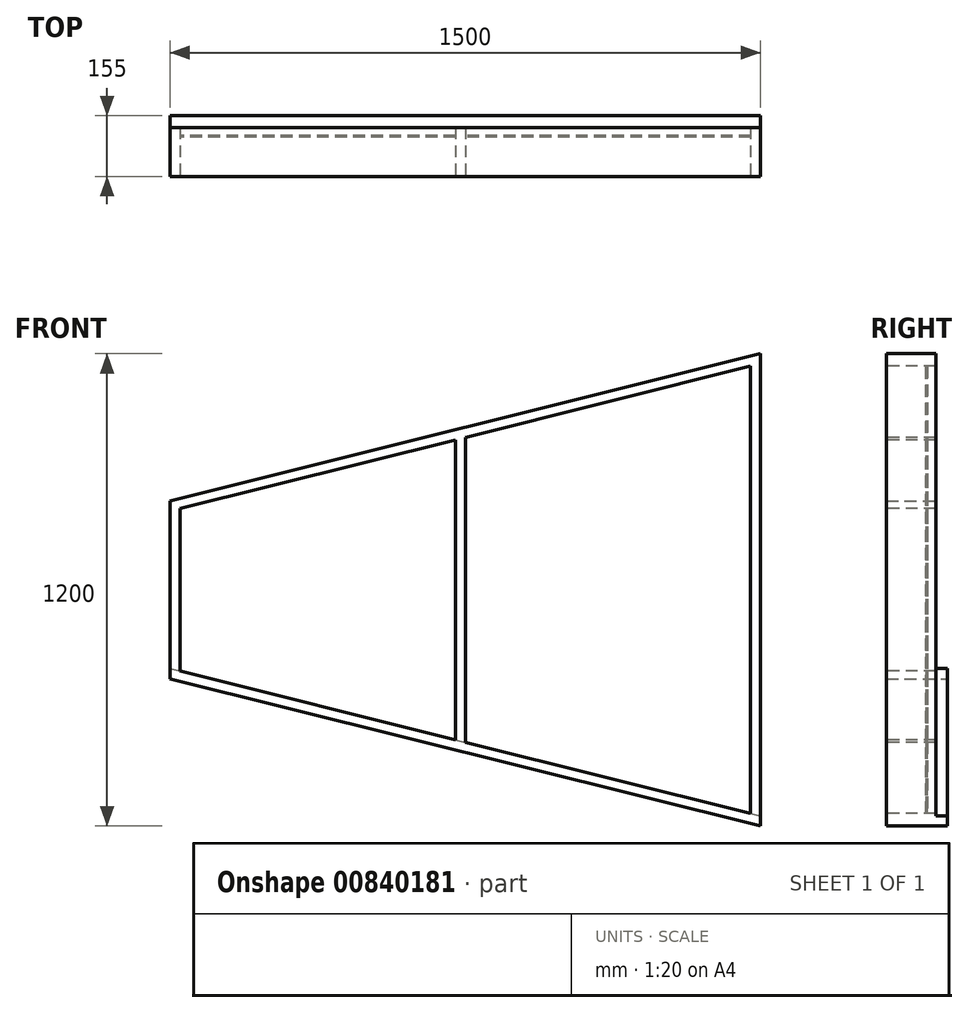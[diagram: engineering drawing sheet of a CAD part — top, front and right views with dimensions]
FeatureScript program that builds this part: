
annotation { "Feature Type Name" : "Feature", "Feature Type Description" : "" }
export const myFeature = defineFeature(function(context is Context, id is Id, definition is map)
    precondition{}
    {
        {
            var Q0;
            Q0=qCreatedBy(makeId("Front.planeOp"),FACE);
            var sketch = newSketch(context, id + "F0", { "sketchPlane" : qUnion([Q0])});
            skLineSegment(sketch, "E0", {"start": v(0, 0) * mm, "end": v(0, 1200) * mm});
            skLineSegment(sketch, "E1", {"start": v(0, 1200) * mm, "end": v(-1500, 826) * mm});
            skLineSegment(sketch, "E2", {"start": v(-1500, 826) * mm, "end": v(-1500, 374) * mm});
            skLineSegment(sketch, "E3", {"start": v(-1500, 374) * mm, "end": v(0, 0) * mm});
            skSolve(sketch);
        }
        {
            var Q0;
            Q0 = qSketchRegion(id + "F0", true);
            extrude(context, id + "F1", {"entities" : qUnion([Q0]), "depth" : 125 * mm, "offsetDistance" : 25 * mm});
        }
        {
            var Q0;
            Q0=makeQuery(id+"F1.opExtrude","CAP_FACE",FACE,{"disambiguationData":[OSD([sQuery(id+"F0.wireOp",EDGE,"E0"),sQuery(id+"F0.wireOp",EDGE,"E1"),sQuery(id+"F0.wireOp",EDGE,"E2"),sQuery(id+"F0.wireOp",EDGE,"E3")])],"isStart":false});
            var sketch = newSketch(context, id + "F2", { "sketchPlane" : qUnion([Q0])});
            skLineSegment(sketch, "E4.0", {"start": v(-25, 1168) * mm, "end": v(-750, 987.24) * mm});
            skLineSegment(sketch, "E4.1", {"start": v(-25, 32) * mm, "end": v(-25, 1168) * mm});
            skLineSegment(sketch, "E4.2", {"start": v(-1475, 393.52) * mm, "end": v(-775, 219) * mm});
            skLineSegment(sketch, "E4.3", {"start": v(-1475, 806.48) * mm, "end": v(-1475, 393.52) * mm});
            skLineSegment(sketch, "E5", {"start": v(-775, 981) * mm, "end": v(-775, 219) * mm});
            skLineSegment(sketch, "E6", {"start": v(-750, 987.24) * mm, "end": v(-750, 212.76) * mm});
            skLineSegment(sketch, "E7.trimOffspring", {"start": v(-775, 981) * mm, "end": v(-1475, 806.48) * mm});
            skLineSegment(sketch, "E8.trimOffspring", {"start": v(-750, 212.76) * mm, "end": v(-25, 32) * mm});
            skSolve(sketch);
        }
        {
            var Q0;
            Q0 = qSketchRegion(id + "F2", true);
            extrude(context, id + "F3", {"entities" : qUnion([Q0]), "operationType" : NewBodyOperationType.REMOVE, "oppositeDirection" : true, "depth" : 50 * mm, "offsetDistance" : 25 * mm});
        }
        {
            var Q0;
            Q0=makeQuery(id+"F1.opExtrude","CAP_FACE",FACE,{"disambiguationData":[OSD([sQuery(id+"F0.wireOp",EDGE,"E0"),sQuery(id+"F0.wireOp",EDGE,"E1"),sQuery(id+"F0.wireOp",EDGE,"E2"),sQuery(id+"F0.wireOp",EDGE,"E3")])],"isStart":true});
            var sketch = newSketch(context, id + "F4", { "sketchPlane" : qUnion([Q0])});
            skLineSegment(sketch, "E9.0", {"start": v(25, 1168) * mm, "end": v(750, 987.24) * mm});
            skLineSegment(sketch, "E9.1", {"start": v(25, 32) * mm, "end": v(25, 1168) * mm});
            skLineSegment(sketch, "E9.2", {"start": v(1475, 393.52) * mm, "end": v(775, 219) * mm});
            skLineSegment(sketch, "E9.3", {"start": v(1475, 806.48) * mm, "end": v(1475, 393.52) * mm});
            skLineSegment(sketch, "E9.4", {"start": v(775, 981) * mm, "end": v(775, 219) * mm});
            skLineSegment(sketch, "E9.5", {"start": v(750, 987.24) * mm, "end": v(750, 212.76) * mm});
            skLineSegment(sketch, "E9.6", {"start": v(775, 981) * mm, "end": v(1475, 806.48) * mm});
            skLineSegment(sketch, "E9.7", {"start": v(750, 212.76) * mm, "end": v(25, 32) * mm});
            skSolve(sketch);
        }
        {
            var Q0;
            Q0 = qSketchRegion(id + "F4", true);
            extrude(context, id + "F5", {"entities" : qUnion([Q0]), "operationType" : NewBodyOperationType.REMOVE, "endBound" : BoundingType.THROUGH_ALL, "oppositeDirection" : true, "depth" : 21 * mm, "offsetDistance" : 25 * mm});
        }
        {
            var Q0;
            Q0=qCreatedBy(makeId("Front.planeOp"),FACE);
            cPlane(context, id + "F6", {"entities" : qUnion([Q0]), "cplaneType" : CPlaneType.OFFSET, "offset" : 25 * mm, "width" : 150 * mm, "height" : 150 * mm});
        }
        {
            var Q0;
            Q0=qCreatedBy(id+"F6.planeOp",FACE);
            var sketch = newSketch(context, id + "F7", { "sketchPlane" : qUnion([Q0])});
            skLineSegment(sketch, "E10.0", {"start": v(-25, 1168) * mm, "end": v(-750, 987.24) * mm});
            skLineSegment(sketch, "E10.1", {"start": v(-750, 987.24) * mm, "end": v(-750, 212.76) * mm});
            skLineSegment(sketch, "E10.2", {"start": v(-750, 212.76) * mm, "end": v(-25, 32) * mm});
            skLineSegment(sketch, "E10.3", {"start": v(-25, 32) * mm, "end": v(-25, 1168) * mm});
            skLineSegment(sketch, "E11.0", {"start": v(-775, 981) * mm, "end": v(-1475, 806.48) * mm});
            skLineSegment(sketch, "E11.1", {"start": v(-775, 981) * mm, "end": v(-775, 219) * mm});
            skLineSegment(sketch, "E11.2", {"start": v(-1475, 806.48) * mm, "end": v(-1475, 393.52) * mm});
            skLineSegment(sketch, "E11.3", {"start": v(-1475, 393.52) * mm, "end": v(-775, 219) * mm});
            skSolve(sketch);
        }
        {
            var Q0;
            Q0=makeQuery(id+"F1.opExtrude","CAP_FACE",FACE,{"disambiguationData":[OSD([sQuery(id+"F0.wireOp",EDGE,"E0"),sQuery(id+"F0.wireOp",EDGE,"E1"),sQuery(id+"F0.wireOp",EDGE,"E2"),sQuery(id+"F0.wireOp",EDGE,"E3")])],"isStart":true});
            var sketch = newSketch(context, id + "F8", { "sketchPlane" : qUnion([Q0])});
            skLineSegment(sketch, "E12.0", {"start": v(750, 212.76) * mm, "end": v(25, 32) * mm});
            skLineSegment(sketch, "E12.1", {"start": v(1500, 374) * mm, "end": v(0, 0) * mm});
            skLineSegment(sketch, "E13", {"start": v(25, 32) * mm, "end": v(0, 25.77) * mm});
            skLineSegment(sketch, "E14", {"start": v(0, 25.77) * mm, "end": v(0, 0) * mm});
            skLineSegment(sketch, "E15", {"start": v(750, 212.76) * mm, "end": v(1500, 399.76) * mm});
            skLineSegment(sketch, "E16", {"start": v(1500, 399.76) * mm, "end": v(1500, 374) * mm});
            skSolve(sketch);
        }
        {
            var Q0;
            Q0 = qSketchRegion(id + "F8", true);
            extrude(context, id + "F9", {"entities" : qUnion([Q0]), "operationType" : NewBodyOperationType.ADD, "depth" : 30 * mm, "offsetDistance" : 25 * mm});
        }
        {
            var Q0;
            Q0=makeQuery(id+"F9.opExtrude","SWEPT_EDGE",EDGE,{"disambiguationData":[OSD([sQuery(id+"F0.wireOp",EDGE,"E2"),sQuery(id+"F8.wireOp",EDGE,"E15"),sQuery(id+"F8.wireOp",EDGE,"E16")])]});
            var Q1;
            Q1=makeQuery(id+"F9.opExtrude","CAP_EDGE",EDGE,{"disambiguationData":[OSD([sQuery(id+"F8.wireOp",EDGE,"E12.0"),sQuery(id+"F8.wireOp",EDGE,"E13"),sQuery(id+"F8.wireOp",EDGE,"E15")])],"isStart":false});
            cPlane(context, id + "F10", {"entities" : qUnion([Q0, Q1]), "cplaneType" : CPlaneType.LINE_ANGLE, "offset" : 25 * mm, "angle" : 90 * degree, "width" : 150 * mm, "height" : 150 * mm});
        }
        {
            var Q0;
            Q0=qCreatedBy(id+"F10.planeOp",FACE);
            var sketch = newSketch(context, id + "F11", { "sketchPlane" : qUnion([Q0])});
            skLineSegment(sketch, "E17.0", {"start": v(30, 25) * mm, "end": v(0, 25) * mm});
            skLineSegment(sketch, "E17.1", {"start": v(30, 25) * mm, "end": v(30, 15) * mm});
            skLineSegment(sketch, "E18", {"start": v(0, 25) * mm, "end": v(30, 15) * mm});
            skPoint(sketch, "E19.orphan", {"position": v(30, 0) * mm});
            skSolve(sketch);
        }
        {
            var Q0;
            Q0 = qSketchRegion(id + "F11", true);
            extrude(context, id + "F12", {"entities" : qUnion([Q0]), "operationType" : NewBodyOperationType.REMOVE, "endBound" : BoundingType.THROUGH_ALL, "depth" : 25 * mm, "offsetDistance" : 25 * mm});
        }
        {
            var Q0;
            Q0=qCreatedBy(id+"F10.planeOp",FACE);
            var sketch = newSketch(context, id + "F13", { "sketchPlane" : qUnion([Q0])});
            skLineSegment(sketch, "E20.bottom", {"start": v(5, 0) * mm, "end": v(2, 0) * mm});
            skLineSegment(sketch, "E20.top", {"start": v(5, 5) * mm, "end": v(2, 5) * mm});
            skLineSegment(sketch, "E20.left", {"start": v(5, 0) * mm, "end": v(5, 5) * mm});
            skLineSegment(sketch, "E20.right", {"start": v(2, 0) * mm, "end": v(2, 5) * mm});
            skSolve(sketch);
        }
        {
            var Q0;
            Q0 = qSketchRegion(id + "F13", true);
            extrude(context, id + "F14", {"entities" : qUnion([Q0]), "operationType" : NewBodyOperationType.REMOVE, "endBound" : BoundingType.THROUGH_ALL, "depth" : 25 * mm, "offsetDistance" : 25 * mm});
        }
        {
            var Q0;
            Q0 = qSketchRegion(id + "F7", true);
            extrude(context, id + "F15", {"entities" : qUnion([Q0]), "oppositeDirection" : true, "depth" : 4 * mm, "offsetDistance" : 25 * mm});
        }
    });
